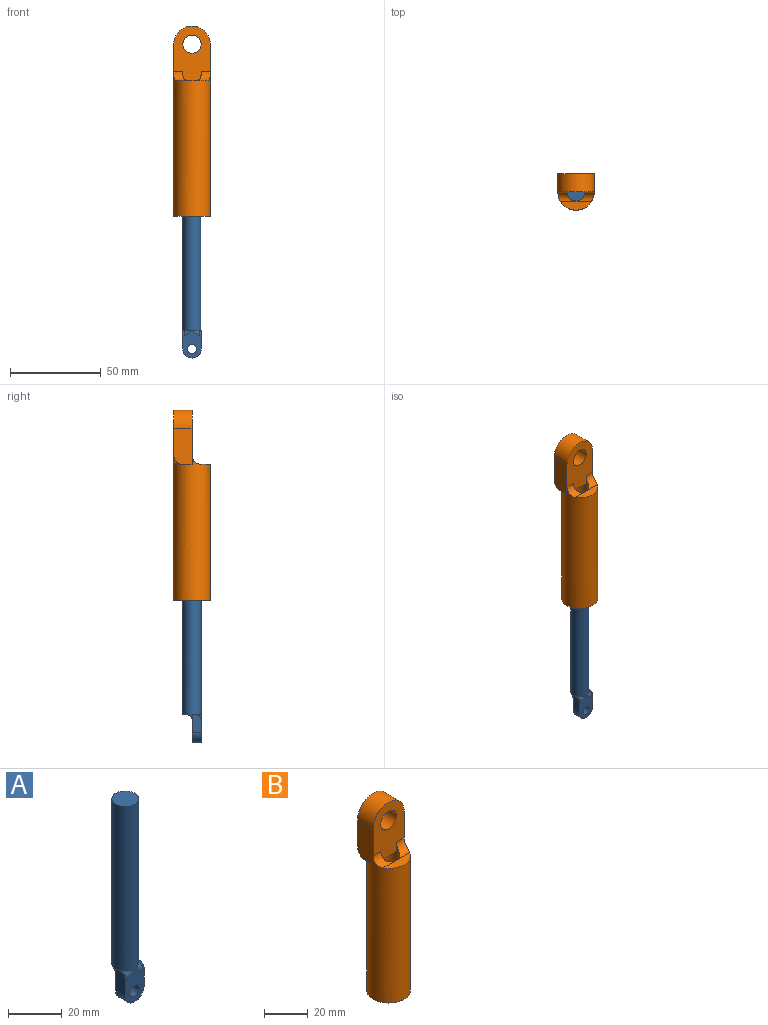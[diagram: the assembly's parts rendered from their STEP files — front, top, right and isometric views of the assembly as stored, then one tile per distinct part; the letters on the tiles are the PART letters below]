
ASSEMBLY  parts=2 mates=1
PART A: 16 faces, bbox 10.1x10.1x90.1 mm
  f0: cylinder r=5mm len=77.5mm, axis (0,0,-1), area 2358.9mm2, adj f1,f2,f3,f4,f5,f7,f12,f13
  f1: plane 10x10mm, normal (0,0,1), area 78.5mm2, adj f0
  f2: plane 8.66x2.5mm, normal (0,0,-1), area 15.4mm2, adj f0,f13
  f3: plane 2.5x0.67mm, normal (0,0,1), area 0.5mm2, adj f0,f7,f11
  f4: plane 2.5x0.67mm, normal (0,0,1), area 0.5mm2, adj f0,f5,f15
  f5: plane 10x5mm, normal (-1,0,0), area 48.7mm2, adj f0,f4,f6,f9,f10,f15
  f6: cylinder r=5mm len=10mm, axis (0,1,0), area 78.5mm2, adj f5,f7,f9,f10
  f7: plane 10x5mm, normal (1,0,0), area 48.7mm2, adj f0,f3,f6,f9,f10,f11
  f8: cylinder r=2.5mm len=5mm, axis (0,1,0), area 78.5mm2, adj f9,f10
  f9: plane 15.11x10.11mm, normal (0,-1,0), area 102.1mm2, adj f5,f6,f7,f8,f11,f12,f14,f15
  f10: plane 12.5x10mm, normal (0,1,0), area 94.6mm2, adj f5,f6,f7,f8,f13
  f11: cylinder r=2.5mm len=2.5mm, axis (1,0,0), area 2.6mm2, adj f3,f7,f9,f12
  f12: bspline ~4.86x2.73mm, area 8.2mm2, adj f0,f9,f11
  f13: cylinder r=2.5mm len=10mm, axis (1,0,0), area 36.6mm2, adj f0,f2,f10
  f14: bspline ~4.86x2.73mm, area 8.4mm2, adj f0,f9,f15
  f15: cylinder r=2.5mm len=2.5mm, axis (1,0,0), area 2.6mm2, adj f4,f5,f9,f14
PART B: 19 faces, bbox 20x20x105 mm
  f0: cylinder r=5mm len=80mm, axis (0,0,1), area 2367.5mm2, adj f1,f5,f12,f15,f16
  f1: plane 20x20mm, normal (0,0,-1), area 235.6mm2, adj f0,f2
  f2: cylinder r=10mm len=80mm, axis (0,0,1), area 4723.2mm2, adj f1,f3,f4,f6,f8,f9,f14,f15
  f3: plane 17.32x5mm, normal (0,0,1), area 61.4mm2, adj f2,f15,f16
  f4: plane 5x1.34mm, normal (0,0,-1), area 2.2mm2, adj f2,f6,f13
  f5: plane 10x5mm, normal (0,0,-1), area 39.3mm2, adj f0,f12
  f6: plane 20x10mm, normal (1,0,0), area 194.6mm2, adj f2,f4,f7,f11,f12,f13
  f7: cylinder r=10mm len=20mm, axis (0,-1,0), area 314.2mm2, adj f6,f8,f11,f12
  f8: plane 20x10mm, normal (-1,0,0), area 194.6mm2, adj f2,f7,f9,f11,f12,f18
  f9: plane 5x1.34mm, normal (0,0,-1), area 2.2mm2, adj f2,f8,f18
  f10: cylinder r=5mm len=10mm, axis (0,-1,0), area 314.2mm2, adj f11,f12
  f11: plane 30x20mm, normal (0,1,0), area 408.4mm2, adj f6,f7,f8,f10,f13,f14,f17,f18
  f12: plane 30x20mm, normal (0,-1,0), area 428.5mm2, adj f0,f5,f6,f7,f8,f10,f15,f16
  f13: cylinder r=5mm len=5mm, axis (-1,0,0), area 10.5mm2, adj f4,f6,f11,f14
  f14: bspline ~9.72x5.45mm, area 33.6mm2, adj f2,f11,f13
  f15: cylinder r=5mm len=10mm, axis (-1,0,0), area 39.7mm2, adj f0,f2,f3,f12
  f16: cylinder r=5mm len=10mm, axis (-1,0,0), area 39.7mm2, adj f0,f2,f3,f12
  f17: bspline ~9.72x5.45mm, area 33.6mm2, adj f2,f11,f18
  f18: cylinder r=5mm len=5mm, axis (-1,0,0), area 10.5mm2, adj f8,f9,f11,f17
PLACE A t=(0,0,100.4)mm
PLACE B t=(0,0,100.7)mm
MATE slider A.f0 <-> B.f0  axis (0,0,1) through (67.08,0,51.24)mm
